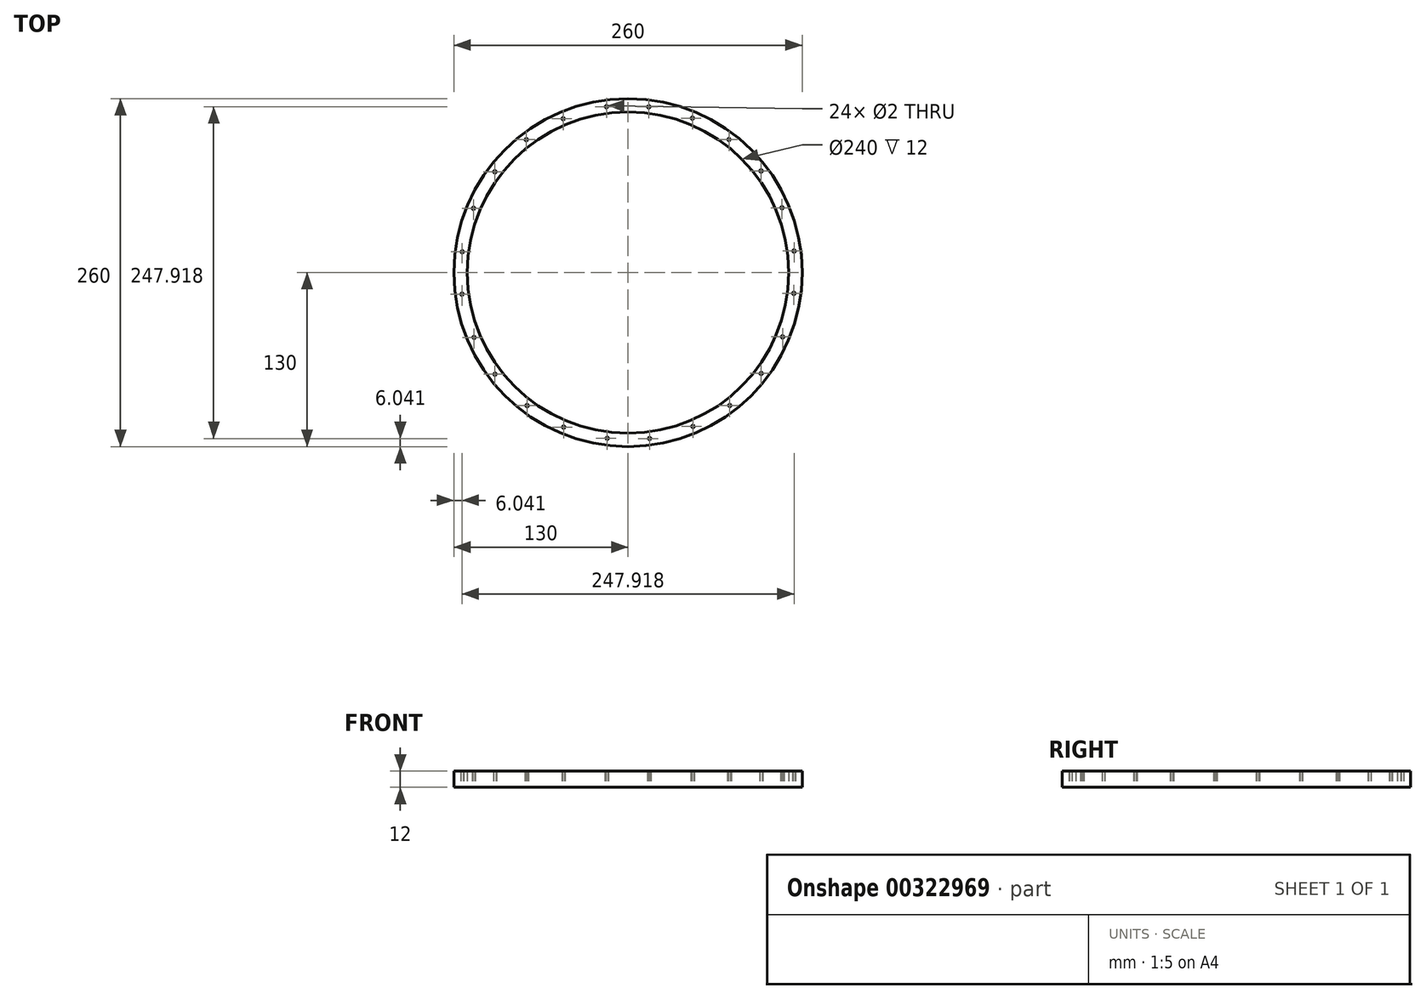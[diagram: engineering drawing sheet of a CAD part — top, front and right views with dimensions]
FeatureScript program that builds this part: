
annotation { "Feature Type Name" : "Feature", "Feature Type Description" : "" }
export const myFeature = defineFeature(function(context is Context, id is Id, definition is map)
    precondition{}
    {
        {
            var Q0;
            Q0=qCreatedBy(makeId("Top.planeOp"),FACE);
            var sketch = newSketch(context, id + "F0", { "sketchPlane" : qUnion([Q0])});
            skCircle(sketch, "E0", {"center": v(0, 0) * mm, "radius": 130 * mm});
            skCircle(sketch, "E1", {"center": v(0, 0) * mm, "radius": 120 * mm});
            skCircle(sketch, "E2", {"center": v(0, 0) * mm, "radius": 125 * mm, "construction": true});
            skLineSegment(sketch, "E3.0", {"start": v(99.3, 75.92) * mm, "end": v(123.96, 16.1) * mm, "construction": true});
            skLineSegment(sketch, "E3.1", {"start": v(123.96, 16.1) * mm, "end": v(115.4, -48.04) * mm, "construction": true});
            skLineSegment(sketch, "E3.2", {"start": v(115.4, -48.04) * mm, "end": v(75.92, -99.3) * mm, "construction": true});
            skLineSegment(sketch, "E3.3", {"start": v(75.92, -99.3) * mm, "end": v(16.1, -123.96) * mm, "construction": true});
            skLineSegment(sketch, "E3.4", {"start": v(16.1, -123.96) * mm, "end": v(-48.04, -115.4) * mm, "construction": true});
            skLineSegment(sketch, "E3.5", {"start": v(-48.04, -115.4) * mm, "end": v(-99.3, -75.92) * mm, "construction": true});
            skLineSegment(sketch, "E3.6", {"start": v(-99.3, -75.92) * mm, "end": v(-123.96, -16.1) * mm, "construction": true});
            skLineSegment(sketch, "E3.7", {"start": v(-123.96, -16.1) * mm, "end": v(-115.4, 48.04) * mm, "construction": true});
            skLineSegment(sketch, "E3.8", {"start": v(-115.4, 48.04) * mm, "end": v(-75.92, 99.3) * mm, "construction": true});
            skLineSegment(sketch, "E3.9", {"start": v(-75.92, 99.3) * mm, "end": v(-16.1, 123.96) * mm, "construction": true});
            skLineSegment(sketch, "E3.10", {"start": v(-16.1, 123.96) * mm, "end": v(48.04, 115.4) * mm, "construction": true});
            skLineSegment(sketch, "E3.11", {"start": v(48.04, 115.4) * mm, "end": v(99.3, 75.92) * mm, "construction": true});
            skCircle(sketch, "E4", {"center": v(115.4, -48.04) * mm, "radius": 1 * mm});
            skCircle(sketch, "E5", {"center": v(75.92, -99.3) * mm, "radius": 1 * mm});
            skCircle(sketch, "E6", {"center": v(-48.04, -115.4) * mm, "radius": 1 * mm});
            skCircle(sketch, "E7", {"center": v(16.1, -123.96) * mm, "radius": 1 * mm});
            skCircle(sketch, "E8", {"center": v(-99.3, -75.92) * mm, "radius": 1 * mm});
            skCircle(sketch, "E9", {"center": v(-123.96, -16.1) * mm, "radius": 1 * mm});
            skCircle(sketch, "E10", {"center": v(-115.4, 48.04) * mm, "radius": 1 * mm});
            skCircle(sketch, "E11", {"center": v(-75.92, 99.3) * mm, "radius": 1 * mm});
            skCircle(sketch, "E12", {"center": v(-16.1, 123.96) * mm, "radius": 1 * mm});
            skCircle(sketch, "E13", {"center": v(123.96, 16.1) * mm, "radius": 1 * mm});
            skCircle(sketch, "E14", {"center": v(48.04, 115.4) * mm, "radius": 1 * mm});
            skCircle(sketch, "E15", {"center": v(99.3, 75.92) * mm, "radius": 1 * mm});
            skCircle(sketch, "E16.cCircle", {"center": v(0, 0) * mm, "radius": 124.74 * mm, "construction": true});
            skLineSegment(sketch, "E16.0", {"start": v(76.53, -98.5) * mm, "end": v(48.43, -114.96) * mm});
            skLineSegment(sketch, "E16.1", {"start": v(48.43, -114.96) * mm, "end": v(17.02, -123.58) * mm});
            skLineSegment(sketch, "E16.2", {"start": v(17.02, -123.58) * mm, "end": v(-15.54, -123.77) * mm});
            skLineSegment(sketch, "E16.3", {"start": v(-15.54, -123.77) * mm, "end": v(-47.05, -115.53) * mm});
            skLineSegment(sketch, "E16.4", {"start": v(-47.05, -115.53) * mm, "end": v(-75.34, -99.42) * mm});
            skLineSegment(sketch, "E16.5", {"start": v(-75.34, -99.42) * mm, "end": v(-98.5, -76.53) * mm});
            skLineSegment(sketch, "E16.6", {"start": v(-98.5, -76.53) * mm, "end": v(-114.96, -48.43) * mm});
            skLineSegment(sketch, "E16.7", {"start": v(-114.96, -48.43) * mm, "end": v(-123.58, -17.02) * mm});
            skLineSegment(sketch, "E16.8", {"start": v(-123.58, -17.02) * mm, "end": v(-123.77, 15.54) * mm});
            skLineSegment(sketch, "E16.9", {"start": v(-123.77, 15.54) * mm, "end": v(-115.53, 47.05) * mm});
            skLineSegment(sketch, "E16.10", {"start": v(-115.53, 47.05) * mm, "end": v(-99.42, 75.34) * mm});
            skLineSegment(sketch, "E16.11", {"start": v(-99.42, 75.34) * mm, "end": v(-76.53, 98.5) * mm});
            skLineSegment(sketch, "E16.12", {"start": v(-76.53, 98.5) * mm, "end": v(-48.43, 114.96) * mm});
            skLineSegment(sketch, "E16.13", {"start": v(-48.43, 114.96) * mm, "end": v(-17.02, 123.58) * mm});
            skLineSegment(sketch, "E16.14", {"start": v(-17.02, 123.58) * mm, "end": v(15.54, 123.77) * mm});
            skLineSegment(sketch, "E16.15", {"start": v(15.54, 123.77) * mm, "end": v(47.05, 115.53) * mm});
            skLineSegment(sketch, "E16.16", {"start": v(47.05, 115.53) * mm, "end": v(75.34, 99.42) * mm});
            skLineSegment(sketch, "E16.17", {"start": v(75.34, 99.42) * mm, "end": v(98.5, 76.53) * mm});
            skLineSegment(sketch, "E16.18", {"start": v(98.5, 76.53) * mm, "end": v(114.96, 48.43) * mm});
            skLineSegment(sketch, "E16.19", {"start": v(114.96, 48.43) * mm, "end": v(123.58, 17.02) * mm});
            skLineSegment(sketch, "E16.20", {"start": v(123.58, 17.02) * mm, "end": v(123.77, -15.54) * mm});
            skLineSegment(sketch, "E16.21", {"start": v(123.77, -15.54) * mm, "end": v(115.53, -47.05) * mm});
            skLineSegment(sketch, "E16.22", {"start": v(115.53, -47.05) * mm, "end": v(99.42, -75.34) * mm});
            skLineSegment(sketch, "E16.23", {"start": v(99.42, -75.34) * mm, "end": v(76.53, -98.5) * mm});
            skCircle(sketch, "E17", {"center": v(99.42, -75.34) * mm, "radius": 1 * mm});
            skCircle(sketch, "E18", {"center": v(48.43, -114.96) * mm, "radius": 1 * mm});
            skCircle(sketch, "E19", {"center": v(-15.54, -123.77) * mm, "radius": 1 * mm});
            skCircle(sketch, "E20", {"center": v(123.77, -15.54) * mm, "radius": 1 * mm});
            skCircle(sketch, "E21", {"center": v(-75.34, -99.42) * mm, "radius": 1 * mm});
            skCircle(sketch, "E22", {"center": v(-114.96, -48.43) * mm, "radius": 1 * mm});
            skCircle(sketch, "E23", {"center": v(-123.77, 15.54) * mm, "radius": 1 * mm});
            skCircle(sketch, "E24", {"center": v(-99.42, 75.34) * mm, "radius": 1 * mm});
            skCircle(sketch, "E25", {"center": v(-48.43, 114.96) * mm, "radius": 1 * mm});
            skCircle(sketch, "E26", {"center": v(15.54, 123.77) * mm, "radius": 1 * mm});
            skCircle(sketch, "E27", {"center": v(75.34, 99.42) * mm, "radius": 1 * mm});
            skCircle(sketch, "E28", {"center": v(114.96, 48.43) * mm, "radius": 1 * mm});
            skSolve(sketch);
        }
        {
            var Q0;
            Q0=makeQuery(id+"F0.imprint","IMPRINT",FACE,{"disambiguationData":[TD([[makeQuery(id+"F0.imprint","IMPRINT",EDGE,{"derivedFrom":sQuery(id+"F0.wireOp",EDGE,"E0")}),1.0]])]});
            var Q1;
            Q1=makeQuery(id+"F0.imprint","IMPRINT",FACE,{"disambiguationData":[TD([[makeQuery(id+"F0.imprint","IMPRINT",EDGE,{"derivedFrom":sQuery(id+"F0.wireOp",EDGE,"E1")}),-1.0]])]});
            extrude(context, id + "F1", {"entities" : qUnion([Q0, Q1]), "depth" : 12 * mm});
        }
    });
